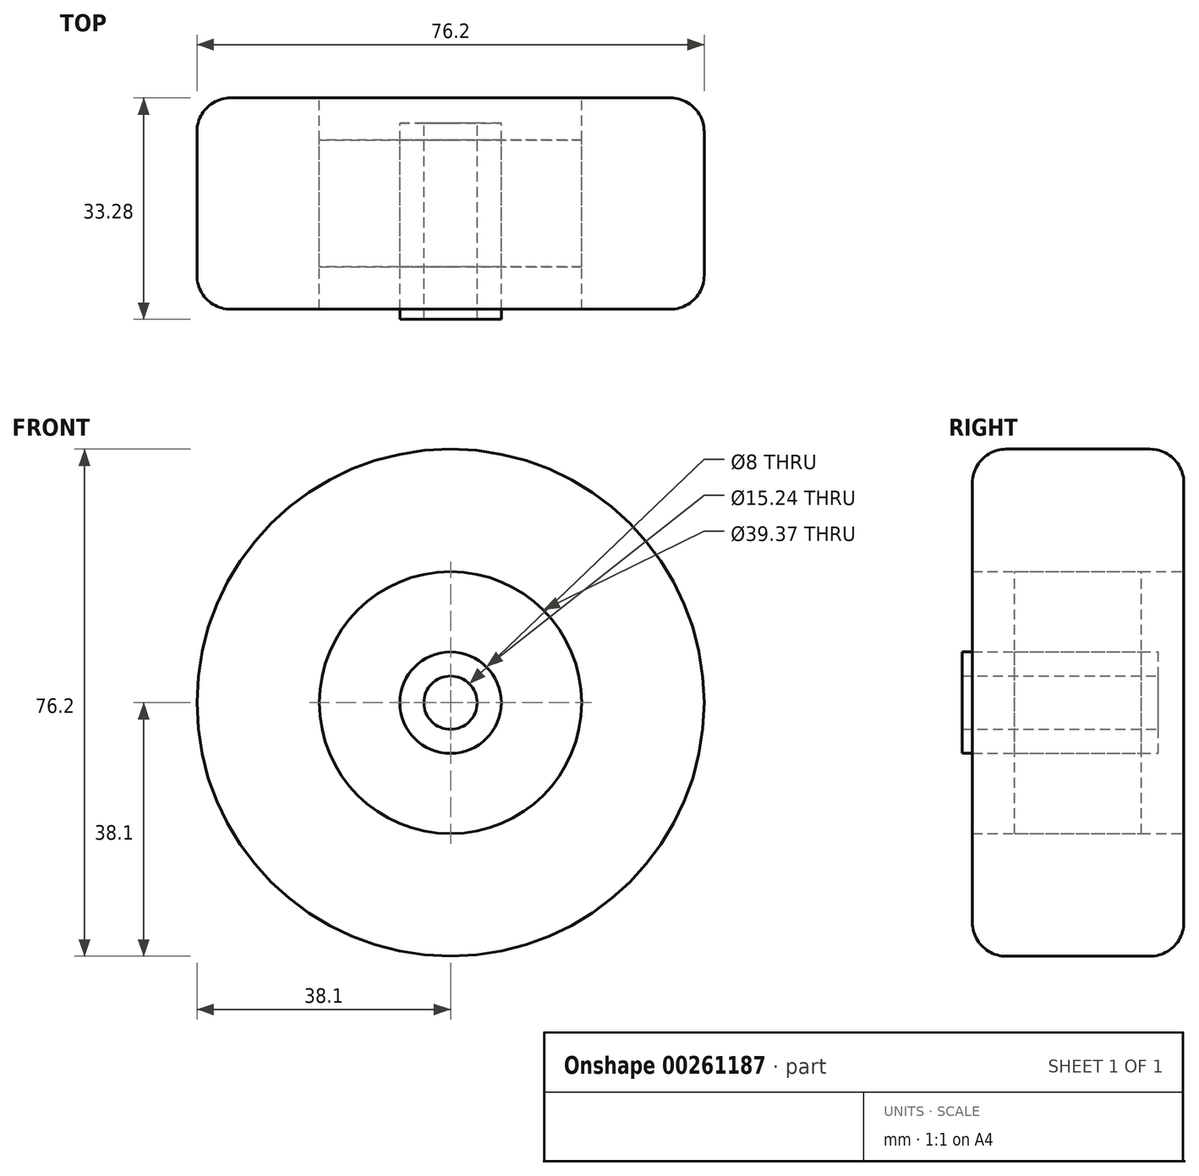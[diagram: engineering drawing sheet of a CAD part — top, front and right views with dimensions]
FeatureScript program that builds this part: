
annotation { "Feature Type Name" : "Feature", "Feature Type Description" : "" }
export const myFeature = defineFeature(function(context is Context, id is Id, definition is map)
    precondition{}
    {
        {
            var Q0;
            Q0=qCreatedBy(makeId("Front.planeOp"),FACE);
            var sketch = newSketch(context, id + "F0", { "sketchPlane" : qUnion([Q0])});
            skCircle(sketch, "E0", {"center": v(0, 0) * mm, "radius": 38.1 * mm});
            skCircle(sketch, "E1", {"center": v(0, 0) * mm, "radius": 4 * mm});
            skCircle(sketch, "E2", {"center": v(0, 0) * mm, "radius": 7.62 * mm});
            skCircle(sketch, "E3", {"center": v(0, 0) * mm, "radius": 8.9 * mm});
            skCircle(sketch, "E4", {"center": v(0, 0) * mm, "radius": 19.69 * mm});
            skSolve(sketch);
        }
        {
            var Q0;
            Q0=makeQuery(id+"F0.imprint","IMPRINT",FACE,{"disambiguationData":[TD([[makeQuery(id+"F0.imprint","IMPRINT",EDGE,{"derivedFrom":sQuery(id+"F0.wireOp",EDGE,"E0")}),1.0]])]});
            extrude(context, id + "F1", {"entities" : qUnion([Q0]), "endBound" : BoundingType.SYMMETRIC, "depth" : 31.75 * mm});
        }
        {
            var Q0;
            Q0=makeQuery(id+"F0.imprint","IMPRINT",FACE,{"disambiguationData":[TD([[makeQuery(id+"F0.imprint","IMPRINT",EDGE,{"derivedFrom":sQuery(id+"F0.wireOp",EDGE,"E1")}),-1.0]])]});
            extrude(context, id + "F2", {"entities" : qUnion([Q0]), "endBound" : BoundingType.SYMMETRIC, "depth" : 24.13 * mm});
        }
        {
            var Q0;
            Q0=makeQuery(id+"F0.imprint","IMPRINT",FACE,{"disambiguationData":[TD([[makeQuery(id+"F0.imprint","IMPRINT",EDGE,{"derivedFrom":sQuery(id+"F0.wireOp",EDGE,"E3")}),-1.0]])]});
            var Q1;
            Q1=makeQuery(id+"F0.imprint","IMPRINT",FACE,{"disambiguationData":[TD([[makeQuery(id+"F0.imprint","IMPRINT",EDGE,{"derivedFrom":sQuery(id+"F0.wireOp",EDGE,"E2")}),-1.0]])]});
            extrude(context, id + "F3", {"entities" : qUnion([Q0, Q1]), "endBound" : BoundingType.SYMMETRIC, "depth" : 19.05 * mm});
        }
        {
            var Q0;
            Q0=makeQuery(id+"F2.opExtrude","CAP_FACE",FACE,{"disambiguationData":[OSD([sQuery(id+"F0.wireOp",EDGE,"E1"),sQuery(id+"F0.wireOp",EDGE,"E2")])],"isStart":false});
            var sketch = newSketch(context, id + "F4", { "sketchPlane" : qUnion([Q0])});
            skCircle(sketch, "E5", {"center": v(0, 0) * mm, "radius": 7.62 * mm});
            skCircle(sketch, "E6", {"center": v(0, 0) * mm, "radius": 4 * mm});
            skSolve(sketch);
        }
        {
            var Q0;
            Q0=makeQuery(id+"F4.imprint","IMPRINT",FACE,{"disambiguationData":[TD([[makeQuery(id+"F4.imprint","IMPRINT",EDGE,{"derivedFrom":sQuery(id+"F4.wireOp",EDGE,"E5")}),1.0]])]});
            extrude(context, id + "F5", {"entities" : qUnion([Q0]), "operationType" : NewBodyOperationType.ADD, "depth" : 5.33 * mm});
        }
        {
            var Q0;
            Q0=makeQuery(id+"F1.opExtrude","CAP_EDGE",EDGE,{"disambiguationData":[OSD([sQuery(id+"F0.wireOp",EDGE,"E0")])],"isStart":false});
            var Q1;
            Q1=makeQuery(id+"F1.opExtrude","CAP_EDGE",EDGE,{"disambiguationData":[OSD([sQuery(id+"F0.wireOp",EDGE,"E0")])],"isStart":true});
            fillet(context, id + "F6", {"entities" : qUnion([Q0, Q1]), "radius" : 5.08 * mm, "tangentPropagation" : true, "allowEdgeOverflow" : false});
        }
    });
